# Revit family: D9505-DN20-RFA_2019
name_source: partatom
category: Pipe Accessories
units: mm (PartAtom-declared; Revit-internal decimal feet)

## family parameters
Always vertical = Yes
Cut with Voids When Loaded = No
Part Type = Valve - Breaks Into
Round Connector Dimension = Use Diameter
Shared = No
Work Plane-Based = No

## types (7) — shared parameters
CAT0 = Yes
H4 = 20 mm  [stored 0.0656168 ft]
HWR = 35 mm  [stored 0.114829 ft]
L2D = 77 mm
L2D_Min = 3048 mm
L3 = 10 mm  [stored 0.0328084 ft]
L6 = 2 mm  [stored 0.00656168 ft]
L7 = 36 mm  [stored 0.11811 ft]
Manufacturer = Hydronic Systems Prague s.r.o.
NUT1 = No
QmdConnectorList = 301;D;302;D
R5 = 20 mm  [stored 0.0656168 ft]
R6 = 8 mm  [stored 0.0262467 ft]
R7 = 9 mm  [stored 0.0295276 ft]
Type Comments = závitový; PN25 (-10~+100°C) nebo PN20 (-10~+130°C)
URL = http://www.hydronic.cz
W2D = 10 mm  [stored 0.0328084 ft]
magiPartTypeId = 304
magiProductFamilyId = 283409d322044e8dba8a30d68fed8b

## per-type parameters (varying)
- D9505 DN10: CenSd_RN2_6=11 mm  [stored 0.0360892 ft]; CenSd_RN_6=14 mm  [stored 0.0459318 ft]; D=10 mm; Description=Ruční vyvažovací ventil závitový; bronzový; DN10; kvs0,97; H1=4 mm  [stored 0.0131234 ft]; H2=42 mm; H3=14 mm  [stored 0.0459318 ft]; H5=13 mm  [stored 0.0426509 ft]; H6=18 mm  [stored 0.0590551 ft]; H7=11 mm  [stored 0.0360892 ft]; H8=27 mm; L1=7 mm  [stored 0.0229659 ft]; L1__ve=-7 mm  [stored -0.0229659 ft]; L2=8 mm  [stored 0.0262467 ft]; L2__ve=-8 mm  [stored -0.0262467 ft]; L4=10 mm  [stored 0.0328084 ft]; L_2=39 mm  [stored 0.127953 ft]; MC Product Code=9505 010 (DN10; PN25 kvs0,97); R1=10 mm  [stored 0.0328084 ft]; R2=13 mm  [stored 0.0426509 ft]; R3=11 mm  [stored 0.0360892 ft]; R4=11 mm  [stored 0.0360892 ft]; RN=16 mm; RN2=13 mm  [stored 0.0426509 ft]; magiProductId=f06221e9bc9341508f66871c80ccb9
- D9505 DN15: CenSd_RN2_6=13 mm  [stored 0.0426509 ft]; CenSd_RN_6=15 mm  [stored 0.0492126 ft]; D=15 mm; Description=Ruční vyvažovací ventil závitový; bronzový; DN15; kvs2,67; H1=5 mm  [stored 0.0164042 ft]; H2=41 mm  [stored 0.134514 ft]; H3=12 mm  [stored 0.0393701 ft]; H5=14 mm  [stored 0.0459318 ft]; H6=19 mm; H7=11 mm  [stored 0.0360892 ft]; H8=27 mm; L1=8 mm  [stored 0.0262467 ft]; L1__ve=-8 mm  [stored -0.0262467 ft]; L2=8 mm  [stored 0.0262467 ft]; L2__ve=-8 mm  [stored -0.0262467 ft]; L4=12 mm  [stored 0.0393701 ft]; L_2=45 mm; MC Product Code=9505 015 (DN15; PN25 kvs2,67); R1=11 mm  [stored 0.0360892 ft]; R2=15 mm  [stored 0.0492126 ft]; R3=12 mm  [stored 0.0393701 ft]; R4=12 mm  [stored 0.0393701 ft]; RN=18 mm  [stored 0.0590551 ft]; RN2=15 mm  [stored 0.0492126 ft]; magiProductId=7168eb0cb4024df38c6d32127ca87d
- D9505 DN20: CenSd_RN2_6=14 mm  [stored 0.0459318 ft]; CenSd_RN_6=17 mm  [stored 0.0557743 ft]; D=20 mm; Description=Ruční vyvažovací ventil závitový; bronzový; DN20; kvs4,1; H1=6 mm  [stored 0.019685 ft]; H2=40 mm  [stored 0.131234 ft]; H3=12 mm  [stored 0.0393701 ft]; H5=16 mm; H6=21 mm; H7=11 mm  [stored 0.0360892 ft]; H8=27 mm; L1=9 mm  [stored 0.0295276 ft]; L1__ve=-9 mm  [stored -0.0295276 ft]; L2=8 mm  [stored 0.0262467 ft]; L2__ve=-8 mm  [stored -0.0262467 ft]; L4=13 mm  [stored 0.0426509 ft]; L_2=51 mm; MC Product Code=9505 020 (DN20; PN25 kvs4,1); R1=13 mm  [stored 0.0426509 ft]; R2=16 mm; R3=14 mm  [stored 0.0459318 ft]; R4=14 mm  [stored 0.0459318 ft]; RN=20 mm  [stored 0.0656168 ft]; RN2=17 mm  [stored 0.0557743 ft]; magiProductId=82f2a7b1fa884f8cafe37fee21fa09
- D9505 DN25: CenSd_RN2_6=16 mm; CenSd_RN_6=19 mm; D=25 mm; Description=Ruční vyvažovací ventil závitový; bronzový; DN25; kvs6,4; H1=7 mm  [stored 0.0229659 ft]; H2=39 mm  [stored 0.127953 ft]; H3=12 mm  [stored 0.0393701 ft]; H5=17 mm  [stored 0.0557743 ft]; H6=22 mm  [stored 0.0721785 ft]; H7=11 mm  [stored 0.0360892 ft]; H8=27 mm; L1=10 mm  [stored 0.0328084 ft]; L1__ve=-10 mm  [stored -0.0328084 ft]; L2=9 mm  [stored 0.0295276 ft]; L2__ve=-9 mm  [stored -0.0295276 ft]; L4=14 mm  [stored 0.0459318 ft]; L_2=55 mm; MC Product Code=9505 025 (DN25; PN25 kvs6,4); R1=14 mm  [stored 0.0459318 ft]; R2=18 mm  [stored 0.0590551 ft]; R3=15 mm  [stored 0.0492126 ft]; R4=15 mm  [stored 0.0492126 ft]; RN=21 mm; RN2=18 mm  [stored 0.0590551 ft]; magiProductId=a5bafb2d780d49b5957b650150642c
- D9505 DN32: CenSd_RN2_6=18 mm  [stored 0.0590551 ft]; CenSd_RN_6=21 mm; D=32 mm; Description=Ruční vyvažovací ventil závitový; bronzový; DN32; kvs12,0; H1=8 mm  [stored 0.0262467 ft]; H2=38 mm  [stored 0.124672 ft]; H3=53 mm; H5=19 mm; H6=24 mm  [stored 0.0787402 ft]; H7=14 mm  [stored 0.0459318 ft]; H8=35 mm  [stored 0.114829 ft]; L1=11 mm  [stored 0.0360892 ft]; L1__ve=-11 mm  [stored -0.0360892 ft]; L2=10 mm  [stored 0.0328084 ft]; L2__ve=-10 mm  [stored -0.0328084 ft]; L4=16 mm; L_2=61 mm; MC Product Code=9505 032 (DN32; PN25 kvs12,0); R1=16 mm; R2=20 mm  [stored 0.0656168 ft]; R3=17 mm  [stored 0.0557743 ft]; R4=17 mm  [stored 0.0557743 ft]; RN=24 mm  [stored 0.0787402 ft]; RN2=20 mm  [stored 0.0656168 ft]; magiProductId=a42dead6f7694bcf97a0a9ce0e311e
- D9505 DN40: CenSd_RN2_6=20 mm  [stored 0.0656168 ft]; CenSd_RN_6=24 mm  [stored 0.0787402 ft]; D=40 mm; Description=Ruční vyvažovací ventil závitový; bronzový; DN40; kvs19,5; H1=10 mm  [stored 0.0328084 ft]; H2=36 mm  [stored 0.11811 ft]; H3=53 mm; H5=21 mm; H6=26 mm  [stored 0.0853018 ft]; H7=14 mm  [stored 0.0459318 ft]; H8=35 mm  [stored 0.114829 ft]; L1=13 mm  [stored 0.0426509 ft]; L1__ve=-13 mm  [stored -0.0426509 ft]; L2=10 mm  [stored 0.0328084 ft]; L2__ve=-10 mm  [stored -0.0328084 ft]; L4=18 mm  [stored 0.0590551 ft]; L_2=71 mm; MC Product Code=9505 040 (DN40; PN25 kvs19,5); R1=18 mm  [stored 0.0590551 ft]; R2=23 mm; R3=19 mm; R4=17 mm  [stored 0.0557743 ft]; RN=27 mm; RN2=23 mm; magiProductId=7d52969a8dcd46c581304e64bff261
- D9505 DN50: CenSd_RN2_6=23 mm; CenSd_RN_6=27 mm; D=50 mm; Description=Ruční vyvažovací ventil závitový; bronzový; DN50; kvs29,8; H1=12 mm  [stored 0.0393701 ft]; H2=34 mm  [stored 0.111549 ft]; H3=53 mm; H5=24 mm  [stored 0.0787402 ft]; H6=29 mm  [stored 0.0951444 ft]; H7=14 mm  [stored 0.0459318 ft]; H8=35 mm  [stored 0.114829 ft]; L1=15 mm  [stored 0.0492126 ft]; L1__ve=-15 mm  [stored -0.0492126 ft]; L2=11 mm  [stored 0.0360892 ft]; L2__ve=-11 mm  [stored -0.0360892 ft]; L4=21 mm; L_2=81 mm; MC Product Code=9505 050 (DN50; PN25 kvs29,8); R1=20 mm  [stored 0.0656168 ft]; R2=26 mm  [stored 0.0853018 ft]; R3=22 mm  [stored 0.0721785 ft]; R4=17 mm  [stored 0.0557743 ft]; RN=31 mm; RN2=26 mm  [stored 0.0853018 ft]; magiProductId=2fc06cc644084f6992b3d357430981

note: [stored X ft] marks values corroborated as IEEE doubles in the binary element streams (Revit-internal decimal feet)

## geometry (parser evidence)
native form markers: Sweep x1
no freeform markers — native parametric forms only
